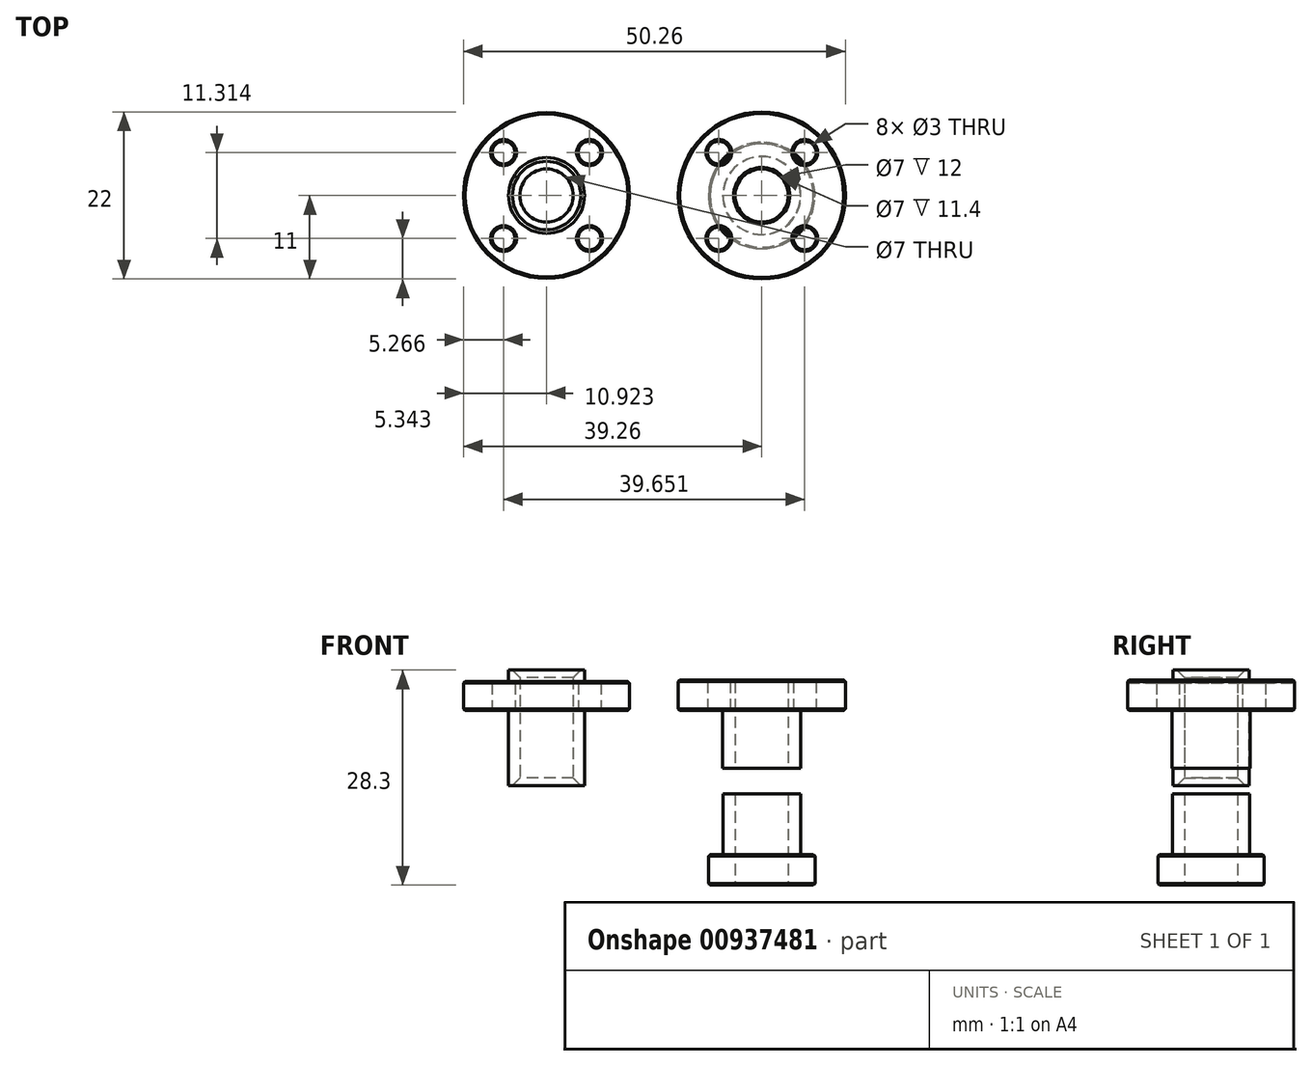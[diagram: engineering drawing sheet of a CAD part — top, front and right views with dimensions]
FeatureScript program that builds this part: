
annotation { "Feature Type Name" : "Feature", "Feature Type Description" : "" }
export const myFeature = defineFeature(function(context is Context, id is Id, definition is map)
    precondition{}
    {
        {
            var Q0;
            Q0=qCreatedBy(makeId("Top.planeOp"),FACE);
            var sketch = newSketch(context, id + "F0", { "sketchPlane" : qUnion([Q0])});
            skCircle(sketch, "E0", {"center": v(-28.34, 0) * mm, "radius": 10.93 * mm});
            skCircle(sketch, "E1", {"center": v(-28.34, 0) * mm, "radius": 3.5 * mm});
            skCircle(sketch, "E2", {"center": v(-22.68, -5.66) * mm, "radius": 1.5 * mm});
            skCircle(sketch, "E3", {"center": v(-22.68, 5.66) * mm, "radius": 1.5 * mm});
            skCircle(sketch, "E4", {"center": v(-34, 5.66) * mm, "radius": 1.5 * mm});
            skCircle(sketch, "E5", {"center": v(-34, -5.66) * mm, "radius": 1.5 * mm});
            skLineSegment(sketch, "E6.trimOffspring", {"start": v(-22.68, 5.66) * mm, "end": v(-28.34, 0) * mm, "construction": true});
            skLineSegment(sketch, "E7.trimOffspring", {"start": v(-34, 5.66) * mm, "end": v(-28.34, 0) * mm, "construction": true});
            skLineSegment(sketch, "E8.trimOffspring", {"start": v(-28.34, 0) * mm, "end": v(-22.68, -5.66) * mm, "construction": true});
            skLineSegment(sketch, "E9.trimOffspring", {"start": v(-28.34, 0) * mm, "end": v(-34, -5.66) * mm, "construction": true});
            skCircle(sketch, "E10", {"center": v(-28.34, 0) * mm, "radius": 5 * mm});
            skLineSegment(sketch, "E11.0", {"start": v(0, 0) * mm, "end": v(0, 0) * mm});
            skLineSegment(sketch, "E11.1", {"start": v(-28.34, 0) * mm, "end": v(-22.68, 5.66) * mm, "construction": true});
            skCircle(sketch, "E12", {"center": v(0, 0) * mm, "radius": 11 * mm});
            skCircle(sketch, "E13", {"center": v(0, 0) * mm, "radius": 3.5 * mm});
            skCircle(sketch, "E14", {"center": v(5.66, -5.66) * mm, "radius": 1.5 * mm});
            skCircle(sketch, "E15", {"center": v(5.66, 5.66) * mm, "radius": 1.5 * mm});
            skCircle(sketch, "E16", {"center": v(-5.66, 5.66) * mm, "radius": 1.5 * mm});
            skCircle(sketch, "E17", {"center": v(-5.66, -5.66) * mm, "radius": 1.5 * mm});
            skLineSegment(sketch, "E18.trimOffspring", {"start": v(5.66, 5.66) * mm, "end": v(0, 0) * mm, "construction": true});
            skLineSegment(sketch, "E19.trimOffspring", {"start": v(-5.66, 5.66) * mm, "end": v(0, 0) * mm, "construction": true});
            skLineSegment(sketch, "E20.trimOffspring", {"start": v(0, 0) * mm, "end": v(5.66, -5.66) * mm, "construction": true});
            skLineSegment(sketch, "E21.trimOffspring", {"start": v(0, 0) * mm, "end": v(-5.66, -5.66) * mm, "construction": true});
            skCircle(sketch, "E22", {"center": v(0, 0) * mm, "radius": 5.15 * mm});
            skLineSegment(sketch, "E23.0", {"start": v(36.51, 2.5) * mm, "end": v(36.51, 2.5) * mm});
            skLineSegment(sketch, "E23.1", {"start": v(0, 0) * mm, "end": v(5.66, 5.66) * mm, "construction": true});
            skSolve(sketch);
        }
        {
            var Q0;
            Q0=makeQuery(id+"F0.imprint","IMPRINT",FACE,{"disambiguationData":[TD([[makeQuery(id+"F0.imprint","IMPRINT",EDGE,{"derivedFrom":sQuery(id+"F0.wireOp",EDGE,"E0")}),1.0]])]});
            extrude(context, id + "F1", {"entities" : qUnion([Q0]), "depth" : 3.8 * mm, "offsetDistance" : 25 * mm});
        }
        {
            var Q0;
            Q0=makeQuery(id+"F0.imprint","IMPRINT",FACE,{"disambiguationData":[TD([[makeQuery(id+"F0.imprint","IMPRINT",EDGE,{"derivedFrom":sQuery(id+"F0.wireOp",EDGE,"E1")}),-1.0]])]});
            extrude(context, id + "F2", {"entities" : qUnion([Q0]), "operationType" : NewBodyOperationType.ADD, "depth" : 5.3 * mm, "offsetDistance" : 25 * mm});
        }
        {
            var Q0;
            Q0=makeQuery(id+"F0.imprint","IMPRINT",FACE,{"disambiguationData":[TD([[makeQuery(id+"F0.imprint","IMPRINT",EDGE,{"derivedFrom":sQuery(id+"F0.wireOp",EDGE,"E1")}),-1.0]])]});
            extrude(context, id + "F3", {"entities" : qUnion([Q0]), "operationType" : NewBodyOperationType.ADD, "oppositeDirection" : true, "depth" : 9.9 * mm, "offsetDistance" : 25 * mm});
        }
        {
            var Q0;
            Q0=makeQuery(id+"F2.opExtrude","CAP_EDGE",EDGE,{"disambiguationData":[OSD([sQuery(id+"F0.wireOp",EDGE,"E1")])],"isStart":false});
            var Q1;
            Q1=makeQuery(id+"F3.opExtrude","CAP_EDGE",EDGE,{"disambiguationData":[OSD([sQuery(id+"F0.wireOp",EDGE,"E1")])],"isStart":false});
            chamfer(context, id + "F4", {"entities" : qUnion([Q0, Q1]), "width" : 1 * mm, "tangentPropagation" : true});
        }
        {
            var Q0;
            Q0=makeQuery(id+"F1.opExtrude","CAP_EDGE",EDGE,{"disambiguationData":[OSD([sQuery(id+"F0.wireOp",EDGE,"E4")])],"isStart":false});
            var Q1;
            Q1=makeQuery(id+"F1.opExtrude","CAP_EDGE",EDGE,{"disambiguationData":[OSD([sQuery(id+"F0.wireOp",EDGE,"E5")])],"isStart":false});
            var Q2;
            Q2=makeQuery(id+"F1.opExtrude","CAP_EDGE",EDGE,{"disambiguationData":[OSD([sQuery(id+"F0.wireOp",EDGE,"E2")])],"isStart":false});
            var Q3;
            Q3=makeQuery(id+"F1.opExtrude","CAP_EDGE",EDGE,{"disambiguationData":[OSD([sQuery(id+"F0.wireOp",EDGE,"E3")])],"isStart":false});
            var Q4;
            Q4=makeQuery(id+"F1.opExtrude","CAP_EDGE",EDGE,{"disambiguationData":[OSD([sQuery(id+"F0.wireOp",EDGE,"E0")])],"isStart":false});
            var Q5;
            Q5=makeQuery(id+"F1.opExtrude","CAP_EDGE",EDGE,{"disambiguationData":[OSD([sQuery(id+"F0.wireOp",EDGE,"E0")])],"isStart":true});
            chamfer(context, id + "F5", {"entities" : qUnion([Q0, Q1, Q2, Q3, Q4, Q5]), "width" : 0.2 * mm, "tangentPropagation" : true});
        }
        {
            var Q0;
            Q0=makeQuery(id+"F0.imprint","IMPRINT",FACE,{"disambiguationData":[TD([[makeQuery(id+"F0.imprint","IMPRINT",EDGE,{"derivedFrom":sQuery(id+"F0.wireOp",EDGE,"E13")}),-1.0]])]});
            var Q1;
            Q1=makeQuery(id+"F0.imprint","IMPRINT",FACE,{"disambiguationData":[TD([[makeQuery(id+"F0.imprint","IMPRINT",EDGE,{"derivedFrom":sQuery(id+"F0.wireOp",EDGE,"E12")}),1.0]])]});
            extrude(context, id + "F6", {"entities" : qUnion([Q0, Q1]), "depth" : 4 * mm, "offsetDistance" : 25 * mm});
        }
        {
            var Q0;
            Q0=makeQuery(id+"F0.imprint","IMPRINT",FACE,{"disambiguationData":[TD([[makeQuery(id+"F0.imprint","IMPRINT",EDGE,{"derivedFrom":sQuery(id+"F0.wireOp",EDGE,"E13")}),-1.0]])]});
            extrude(context, id + "F7", {"entities" : qUnion([Q0]), "operationType" : NewBodyOperationType.ADD, "oppositeDirection" : true, "depth" : 11 * mm, "offsetDistance" : 25 * mm});
        }
        {
            var Q0;
            Q0=makeQuery(id+"F7.opExtrude","CAP_FACE",FACE,{"disambiguationData":[OSD([sQuery(id+"F0.wireOp",EDGE,"E13"),sQuery(id+"F0.wireOp",EDGE,"E22")])],"isStart":false});
            cPlane(context, id + "F8", {"entities" : qUnion([Q0]), "cplaneType" : CPlaneType.OFFSET, "offset" : 12 * mm, "width" : 150 * mm, "height" : 150 * mm});
        }
        {
            var Q0;
            Q0=qCreatedBy(id+"F8.planeOp",FACE);
            var sketch = newSketch(context, id + "F9", { "sketchPlane" : qUnion([Q0])});
            skCircle(sketch, "E24", {"center": v(0, 0) * mm, "radius": 3.5 * mm});
            skCircle(sketch, "E25", {"center": v(0, 0) * mm, "radius": 5.1 * mm});
            skCircle(sketch, "E26", {"center": v(0, 0) * mm, "radius": 7 * mm});
            skSolve(sketch);
        }
        {
            var Q0;
            Q0=makeQuery(id+"F9.imprint","IMPRINT",FACE,{"disambiguationData":[TD([[makeQuery(id+"F9.imprint","IMPRINT",EDGE,{"derivedFrom":sQuery(id+"F9.wireOp",EDGE,"E24")}),-1.0]])]});
            extrude(context, id + "F10", {"entities" : qUnion([Q0]), "oppositeDirection" : true, "depth" : 15.2 * mm, "offsetDistance" : 25 * mm});
        }
        {
            var Q0;
            Q0=makeQuery(id+"F9.imprint","IMPRINT",FACE,{"disambiguationData":[TD([[makeQuery(id+"F9.imprint","IMPRINT",EDGE,{"derivedFrom":sQuery(id+"F9.wireOp",EDGE,"E25")}),-1.0]])]});
            extrude(context, id + "F11", {"entities" : qUnion([Q0]), "operationType" : NewBodyOperationType.ADD, "oppositeDirection" : true, "depth" : 4 * mm, "offsetDistance" : 25 * mm});
        }
        {
            var Q0;
            Q0=qCreatedBy(makeId("Front.planeOp"),FACE);
            var sketch = newSketch(context, id + "F12", { "sketchPlane" : qUnion([Q0])});
            skLineSegment(sketch, "E27.0", {"start": v(-5.15, -11) * mm, "end": v(5.15, -11) * mm});
            skPoint(sketch, "E28", {"position": v(0, -11) * mm});
            skLineSegment(sketch, "E29", {"start": v(-1.8, -11) * mm, "end": v(-1.8, -7.6) * mm});
            skLineSegment(sketch, "E30", {"start": v(-1.8, -7.6) * mm, "end": v(1.8, -7.6) * mm});
            skLineSegment(sketch, "E31", {"start": v(1.8, -7.6) * mm, "end": v(1.8, -11) * mm});
            skLineSegment(sketch, "E32.0", {"start": v(1.6, -7.8) * mm, "end": v(1.6, -11) * mm});
            skLineSegment(sketch, "E32.1", {"start": v(-1.6, -7.8) * mm, "end": v(1.6, -7.8) * mm});
            skLineSegment(sketch, "E32.2", {"start": v(-1.6, -11) * mm, "end": v(-1.6, -7.8) * mm});
            skLineSegment(sketch, "E33", {"start": v(-5.15, -10.8) * mm, "end": v(5.15, -10.8) * mm});
            skLineSegment(sketch, "E34", {"start": v(-5.15, -10.8) * mm, "end": v(-5.15, -11) * mm});
            skLineSegment(sketch, "E35", {"start": v(5.15, -10.8) * mm, "end": v(5.15, -11) * mm});
            skLineSegment(sketch, "E36.bottom", {"start": v(1.8, -7.6) * mm, "end": v(5.15, -7.6) * mm});
            skLineSegment(sketch, "E36.top", {"start": v(1.8, -10.8) * mm, "end": v(5.15, -10.8) * mm});
            skLineSegment(sketch, "E36.left", {"start": v(1.8, -7.6) * mm, "end": v(1.8, -10.8) * mm});
            skLineSegment(sketch, "E36.right", {"start": v(5.15, -7.6) * mm, "end": v(5.15, -10.8) * mm});
            skLineSegment(sketch, "E37", {"start": v(-1.8, -7.6) * mm, "end": v(-5.15, -7.6) * mm});
            skLineSegment(sketch, "E38", {"start": v(-5.15, -7.6) * mm, "end": v(-5.15, -10.8) * mm});
            skSolve(sketch);
        }
        {
            var Q0;
            {var subQ0=sQuery(id+"F12.wireOp",EDGE,"E32.0");Q0=makeQuery(id+"F12.imprint","IMPRINT",FACE,{"disambiguationData":[TD([[makeQuery(id+"F12.imprint","IMPRINT",EDGE,{"derivedFrom":subQ0}),-1.0]])]});}
            var Q1;
            {var subQ0=sQuery(id+"F12.wireOp",EDGE,"E29");Q1=makeQuery(id+"F12.imprint","IMPRINT",FACE,{"disambiguationData":[TD([[makeQuery(id+"F12.imprint","IMPRINT",EDGE,{"derivedFrom":subQ0}),-1.0]])]});}
            var Q2;
            {var subQ5=sQuery(id+"F12.wireOp",EDGE,"E30");Q2=makeQuery(id+"F12.imprint","IMPRINT",FACE,{"disambiguationData":[TD([[makeQuery(id+"F12.imprint","IMPRINT",EDGE,{"derivedFrom":subQ5}),-1.0]])]});}
            var Q3;
            {var subQ0=sQuery(id+"F12.wireOp",EDGE,"E31");var subQ1=sQuery(id+"F12.wireOp",EDGE,"E27.0");var subQ2=makeQuery(id+"F12.imprint","INTERSECT",VERTEX,{"derivedFrom":[subQ1,subQ0]});Q3=makeQuery(id+"F12.imprint","IMPRINT",FACE,{"disambiguationData":[TD([[makeQuery(id+"F12.imprint","IMPRINT",EDGE,{"disambiguationData":[TD([[subQ2,1.0]])],"derivedFrom":subQ1}),1.0]])]});}
            extrude(context, id + "F13", {"entities" : qUnion([Q0, Q1, Q2, Q3]), "operationType" : NewBodyOperationType.REMOVE, "oppositeDirection" : true, "depth" : 25 * mm, "offsetDistance" : 25 * mm, "symmetric" : true});
        }
        {
            var Q0;
            {var subQ4=sQuery(id+"F12.wireOp",EDGE,"E30");Q0=makeQuery(id+"F12.imprint","IMPRINT",FACE,{"disambiguationData":[TD([[makeQuery(id+"F12.imprint","IMPRINT",EDGE,{"derivedFrom":subQ4}),-1.0]])]});}
            var Q1;
            {var subQ0=sQuery(id+"F12.wireOp",EDGE,"E37");Q1=makeQuery(id+"F12.imprint","IMPRINT",FACE,{"disambiguationData":[TD([[makeQuery(id+"F12.imprint","IMPRINT",EDGE,{"derivedFrom":subQ0}),1.0]])]});}
            var Q2;
            Q2=makeQuery(id+"F12.imprint","IMPRINT",FACE,{"disambiguationData":[TD([[makeQuery(id+"F12.imprint","IMPRINT",EDGE,{"derivedFrom":sQuery(id+"F12.wireOp",EDGE,"E36.bottom")}),-1.0]])]});
            var Q3;
            {var subQ0=sQuery(id+"F12.wireOp",EDGE,"E34");Q3=makeQuery(id+"F12.imprint","IMPRINT",FACE,{"disambiguationData":[TD([[makeQuery(id+"F12.imprint","IMPRINT",EDGE,{"derivedFrom":subQ0}),1.0]])]});}
            var Q4;
            {var subQ0=sQuery(id+"F12.wireOp",EDGE,"E29");var subQ1=sQuery(id+"F12.wireOp",EDGE,"E27.0");var subQ2=makeQuery(id+"F12.imprint","INTERSECT",VERTEX,{"derivedFrom":[subQ1,subQ0]});Q4=makeQuery(id+"F12.imprint","IMPRINT",FACE,{"disambiguationData":[TD([[makeQuery(id+"F12.imprint","IMPRINT",EDGE,{"disambiguationData":[TD([[subQ2,-1.0]])],"derivedFrom":subQ1}),1.0]])]});}
            var Q5;
            {var subQ0=sQuery(id+"F12.wireOp",EDGE,"E31");Q5=makeQuery(id+"F12.imprint","IMPRINT",FACE,{"disambiguationData":[TD([[makeQuery(id+"F12.imprint","IMPRINT",EDGE,{"derivedFrom":subQ0}),-1.0]])]});}
            var Q6;
            {var subQ2=sQuery(id+"F12.wireOp",EDGE,"E31");Q6=makeQuery(id+"F12.imprint","IMPRINT",FACE,{"disambiguationData":[TD([[makeQuery(id+"F12.imprint","IMPRINT",EDGE,{"derivedFrom":subQ2}),1.0]])]});}
            extrude(context, id + "F14", {"entities" : qUnion([Q0, Q1, Q2, Q3, Q4, Q5, Q6]), "operationType" : NewBodyOperationType.REMOVE, "oppositeDirection" : true, "depth" : 25 * mm, "offsetDistance" : 25 * mm, "symmetric" : true});
        }
        {
            var Q0;
            Q0=makeQuery(id+"F6.opExtrude","CAP_FACE",FACE,{"disambiguationData":[OSD([sQuery(id+"F0.wireOp",EDGE,"E12"),sQuery(id+"F0.wireOp",EDGE,"E13"),sQuery(id+"F0.wireOp",EDGE,"E14"),sQuery(id+"F0.wireOp",EDGE,"E15"),sQuery(id+"F0.wireOp",EDGE,"E16"),sQuery(id+"F0.wireOp",EDGE,"E17")])],"isStart":false});
            var Q1;
            Q1=makeQuery(id+"F6.opExtrude","CAP_EDGE",EDGE,{"disambiguationData":[OSD([sQuery(id+"F0.wireOp",EDGE,"E12")])],"isStart":true});
            var Q2;
            Q2=makeQuery(id+"F11.opExtrude","CAP_EDGE",EDGE,{"disambiguationData":[OSD([sQuery(id+"F9.wireOp",EDGE,"E26")])],"isStart":false});
            var Q3;
            Q3=makeQuery(id+"F11.opExtrude","CAP_EDGE",EDGE,{"disambiguationData":[OSD([sQuery(id+"F9.wireOp",EDGE,"E26")])],"isStart":true});
            chamfer(context, id + "F15", {"entities" : qUnion([Q0, Q1, Q2, Q3]), "width" : 0.2 * mm, "tangentPropagation" : true});
        }
    });
